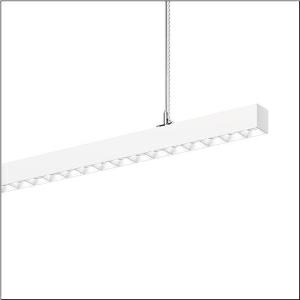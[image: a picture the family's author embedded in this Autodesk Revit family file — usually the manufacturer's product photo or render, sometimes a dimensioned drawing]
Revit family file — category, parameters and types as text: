
# Revit family: silica_r__21_51mx36dc3dwb_b05b
name_source: partatom
category: Lighting Fixtures
units: mm (PartAtom-declared; Revit-internal decimal feet)

## family parameters
Cut with Voids When Loaded = No
Host = Face
Light Source = No
Part Type = Normal
Room Calculation Point = No
Round Connector Dimension = Use Diameter
Shared = No

## types (1)
- --- (1 x LED, 17650 lm, 104.1 W, 3000K)
    Apparent Load = 104 VA
    CIE Flux Codes = 83 98 100 61 100
    Color Rendering = 80
    Color Temperature = 3000K
    Default Elevation = 1800 mm
    Description = Silica® 21, office luminaire, primary light control with darklight reflector, of PMMA, white, CAT 2 (L<= 3000cd/m²), light emission: direct/indirect distribution, primary light characteristic: symmetric, installation type: suspended mounting, LED, rated luminous flux: 17.650lm, luminous efficacy: 170lm/W, light colour: 830, colour temperature: 3000K, with terminal, 3+2-pole, max. 2.5mm², mains connection: 220..240V, AC, 50/60Hz, rated input power: 104.1W, luminaire housing, of aluminium, traffic white (RAL 9016), length: 3.004mm, width: 53mm, height: 53mm, protection rating (complete): IP20, insulation class (complete): insulation class I (protective earthing), certification: CE, permissible operating ambient temperature: 0..+35°C, standard: EN 50419, packaging unit: 1 piece
    Height = 53 mm
    Lamp = 1 x LED
    Lamp Light Flux = 17650 lm
    Lamp Power = 104.1 W
    Lamp count = 1
    Length = 3004 mm
    Luminous efficacy = 170 lm/W
    Manufacturer = Siteco
    ModVariant = No
    Model = 51MX36DC3DWB
    Mounting Place = Ceiling
    Mounting Type = Pendant
    Number of Poles = 1
    OnlyDefault = Yes
    Power Factor = 1
    Product Name = Silica® 21
    Product group = office luminaire | ceiling pendant
    ProductGroupID = 902
    Protection Class = Protection class I
    Protection Degree = IP 20
    RLX_Detail_Level = 1
    RLX_Emergency_Light_Flux = 0 lm
    RLX_Emergency_Type = 0
    RLX_Emergency_Type_DB = No
    RlxData = <blob elided: 61785 chars, md5=ccdda79b>
    Socket = socket
    Standby Power = 0 W
    System Light Flux = 17650 lm
    System Power = 104 W
    Type Comments = factory setting: luminous flux: 100 % | dim-lin: 254 | 359 mA
    Type Image = l_1297797.jpg
    URL = http://relux.com
    VarID = @adj_052133
    Voltage = 0 V
    Weight = 0.00 kg
    Width = 53 mm

## geometry (parser evidence)
native form markers: Blend x4, Sweep x10
no freeform markers — native parametric forms only
